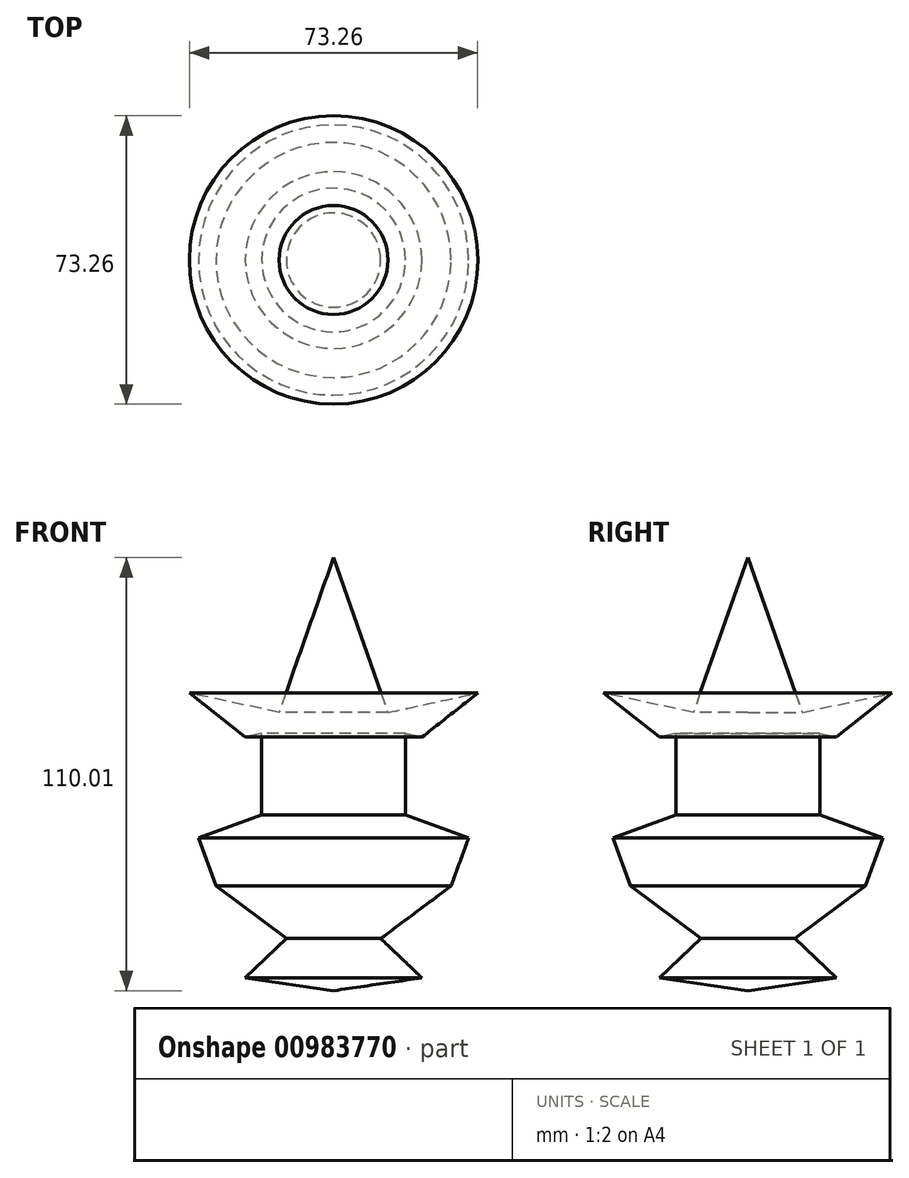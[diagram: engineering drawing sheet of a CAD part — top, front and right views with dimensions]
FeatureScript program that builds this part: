
annotation { "Feature Type Name" : "Feature", "Feature Type Description" : "" }
export const myFeature = defineFeature(function(context is Context, id is Id, definition is map)
    precondition{}
    {
        {
            var Q0;
            Q0=qCreatedBy(makeId("Front.planeOp"),FACE);
            var sketch = newSketch(context, id + "F0", { "sketchPlane" : qUnion([Q0])});
            skLineSegment(sketch, "E0", {"start": v(0, 55.47) * mm, "end": v(0, -54.54) * mm});
            skLineSegment(sketch, "E1", {"start": v(0, 55.47) * mm, "end": v(-13.84, 16.16) * mm});
            skLineSegment(sketch, "E2", {"start": v(-18.26, 10.82) * mm, "end": v(-22.44, 9.88) * mm});
            skLineSegment(sketch, "E3", {"start": v(-36.63, 21.05) * mm, "end": v(-13.84, 16.16) * mm});
            skLineSegment(sketch, "E4", {"start": v(-36.63, 21.05) * mm, "end": v(-22.44, 9.88) * mm});
            skLineSegment(sketch, "E5", {"start": v(-18.26, 10.82) * mm, "end": v(-18.26, -9.88) * mm});
            skLineSegment(sketch, "E6", {"start": v(-18.26, -9.88) * mm, "end": v(-34.3, -15.7) * mm});
            skLineSegment(sketch, "E7", {"start": v(-34.3, -15.7) * mm, "end": v(-29.87, -27.94) * mm});
            skLineSegment(sketch, "E8", {"start": v(-29.87, -27.94) * mm, "end": v(-11.98, -41.28) * mm});
            skLineSegment(sketch, "E9", {"start": v(-11.98, -41.28) * mm, "end": v(-22.44, -51.29) * mm});
            skLineSegment(sketch, "E10", {"start": v(-22.44, -51.29) * mm, "end": v(0, -54.54) * mm});
            skSolve(sketch);
        }
        {
            var Q0;
            Q0=makeQuery(id+"F0.imprint","IMPRINT",FACE,{"disambiguationData":[TD([[makeQuery(id+"F0.imprint","IMPRINT",EDGE,{"derivedFrom":sQuery(id+"F0.wireOp",EDGE,"E0")}),-1.0]])]});
            var Q1;
            Q1=sQuery(id+"F0.wireOp",EDGE,"E0");
            revolve(context, id + "F1", {"surfaceOperationType" : NewSurfaceOperationType.NEW, "entities" : qUnion([Q0]), "axis" : qUnion([Q1]), "revolveType" : RevolveType.FULL});
        }
    });
